# Revit family: Sink-Under_Mount-Kitchen-KOHLER-Bakersfield-K-5832
name_source: partatom
category: Plumbing Fixtures
revit_build: Autodesk Revit 2015 (Build: 20140606_1530(x64)
units: mm (PartAtom-declared; Revit-internal decimal feet)

## types (4) — shared parameters
ADA Compliant = No
Assembly Code = D2010400
CW Connection = No
Cold Water Inlet = Cold Water Inlet
Date Modified = 04/19/2019
Default Elevation = 36"
Description = 31 Inch x 22 Inch x 8-5/8 Inch under-mount single-bowl kitchen sink with 5 faucet holes
Drain Included = No
Flow Rate = 0 GPM
HW Connection = No
Height = 8 5/8"
Hot Water Inlet = Hot Water Inlet
Length = 31"
Manufacturer = KOHLER Co.
MasterFormat 1995 = 15410
MasterFormat 2004 = 22.41.16
Material = Enameled Cast Iron
Pressure = 0.00 psi
Product Documentation Link = https://www.us.kohler.com
Product Name = Bakersfield
Product Page URL = http://www.us.kohler.com
URL = https://www.us.kohler.com
Vent Connection = No
Waste Connection = Yes
Waste Water Outlet = Waste Water Outlet
WaterSense Certified = No
Width = 22"

## per-type parameters (varying)
| type | Finish | Model | Type |
| 0-White | Kohler-Enameled_Cast_Iron-0-White | K-5832-5U-0 | 1 |
| 96-Biscuit | Kohler-Enameled_Cast_Iron-96-Biscuit | K-5832-5U-96 | 2 |
| 47-Almond | Kohler-Enameled_Cast_Iron-47-Almond | K-5832-5U-47 | 3 |
| 7-Black Black | Kohler-Enameled_Cast_Iron-7-Black_Black | K-5832-5U-7 | 4 |

## geometry (parser evidence)
native form markers: Sweep x5
no freeform markers — native parametric forms only
